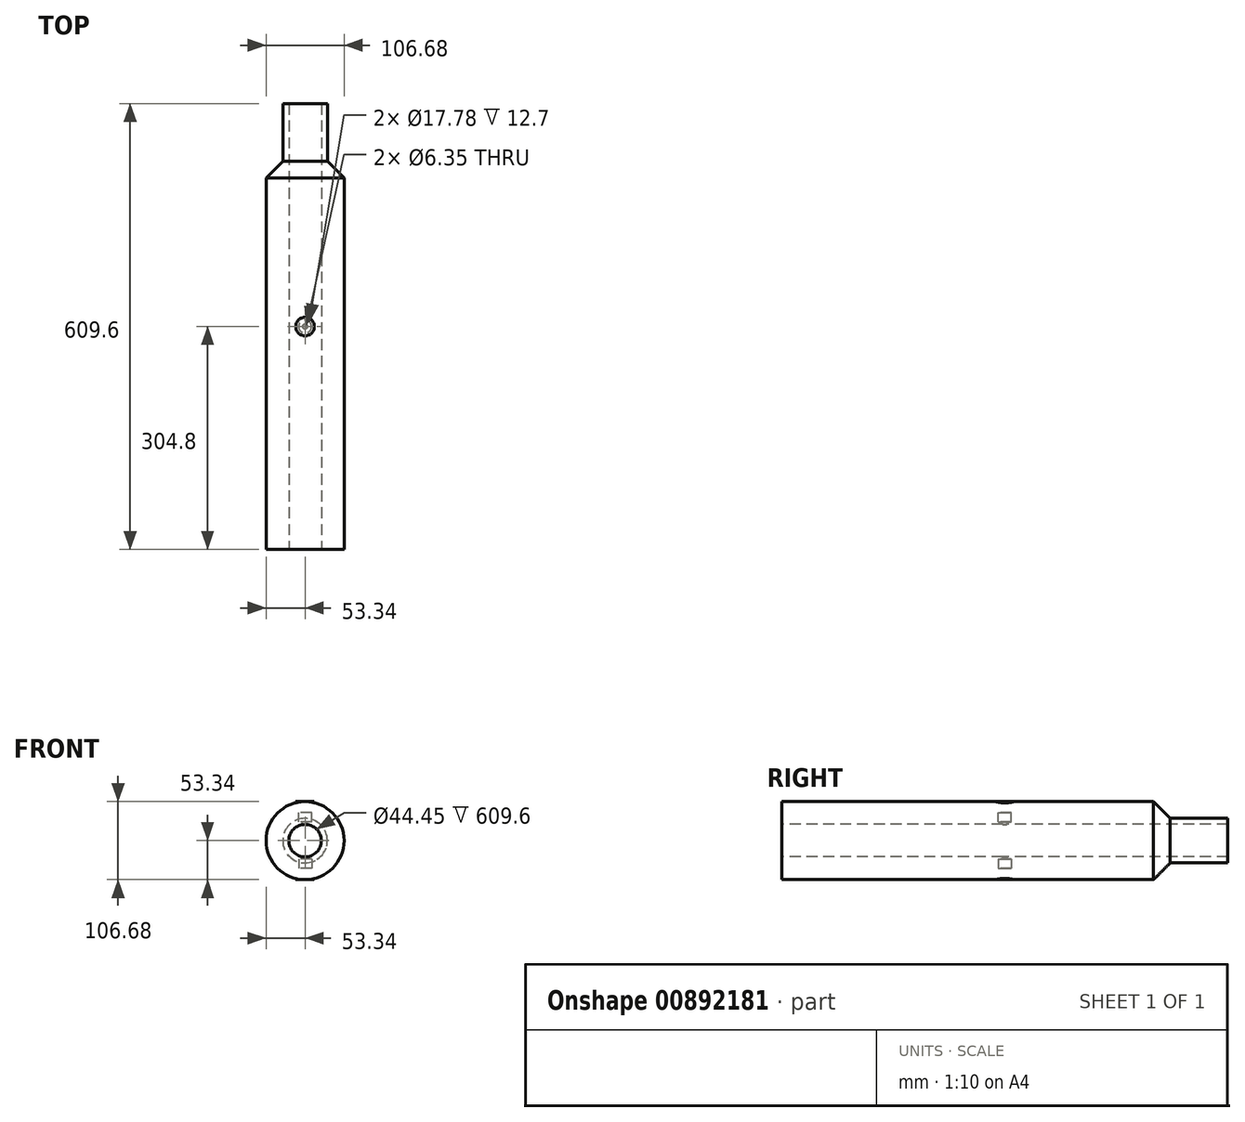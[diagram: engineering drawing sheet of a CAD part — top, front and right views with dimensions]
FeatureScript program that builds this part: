
annotation { "Feature Type Name" : "Feature", "Feature Type Description" : "" }
export const myFeature = defineFeature(function(context is Context, id is Id, definition is map)
    precondition{}
    {
        {
            var Q0;
            Q0=qCreatedBy(makeId("Front.planeOp"),FACE);
            var sketch = newSketch(context, id + "F0", { "sketchPlane" : qUnion([Q0])});
            skCircle(sketch, "E0", {"center": v(0, 0) * mm, "radius": 22.23 * mm});
            skCircle(sketch, "E1", {"center": v(0, 0) * mm, "radius": 53.34 * mm});
            skSolve(sketch);
        }
        {
            var Q0;
            Q0=makeQuery(id+"F0.imprint","IMPRINT",FACE,{"disambiguationData":[TD([[makeQuery(id+"F0.imprint","IMPRINT",EDGE,{"derivedFrom":sQuery(id+"F0.wireOp",EDGE,"E0")}),-1.0]])]});
            extrude(context, id + "F1", {"entities" : qUnion([Q0]), "endBound" : BoundingType.SYMMETRIC, "oppositeDirection" : true, "depth" : 609.6 * mm, "offsetDistance" : 25.4 * mm});
        }
        {
            var Q0;
            Q0=makeQuery(id+"F1.opExtrude","CAP_FACE",FACE,{"disambiguationData":[OSD([sQuery(id+"F0.wireOp",EDGE,"E0"),sQuery(id+"F0.wireOp",EDGE,"E1")])],"isStart":false});
            cPlane(context, id + "F2", {"entities" : qUnion([Q0]), "cplaneType" : CPlaneType.OFFSET, "offset" : 0 * mm, "oppositeDirection" : true, "width" : 152.4 * mm, "height" : 152.4 * mm});
        }
        {
            var Q0;
            Q0=qCreatedBy(makeId("Front.planeOp"),FACE);
            cPlane(context, id + "F3", {"entities" : qUnion([Q0]), "cplaneType" : CPlaneType.OFFSET, "offset" : 203.2 * mm, "oppositeDirection" : true, "width" : 152.4 * mm, "height" : 152.4 * mm});
        }
        {
            var Q0;
            Q0=qCreatedBy(id+"F2.planeOp",FACE);
            var sketch = newSketch(context, id + "F4", { "sketchPlane" : qUnion([Q0])});
            skCircle(sketch, "E2", {"center": v(0, 0) * mm, "radius": 22.23 * mm});
            skCircle(sketch, "E3", {"center": v(0, 0) * mm, "radius": 30.48 * mm});
            skCircle(sketch, "E4", {"center": v(0, 0) * mm, "radius": 53.34 * mm});
            skSolve(sketch);
        }
        {
            var Q0;
            Q0=makeQuery(id+"F4.imprint","IMPRINT",FACE,{"disambiguationData":[TD([[makeQuery(id+"F4.imprint","IMPRINT",EDGE,{"derivedFrom":sQuery(id+"F4.wireOp",EDGE,"E3")}),-1.0]])]});
            var Q1;
            Q1=qCreatedBy(id+"F3.planeOp",FACE);
            extrude(context, id + "F5", {"entities" : qUnion([Q0]), "operationType" : NewBodyOperationType.REMOVE, "oppositeDirection" : true, "depth" : 101.6 * mm, "endBoundEntityFace" : qUnion([Q1]), "offsetDistance" : 25.4 * mm});
        }
        {
            var Q0;
            Q0=qCreatedBy(makeId("Right.planeOp"),FACE);
            var sketch = newSketch(context, id + "F6", { "sketchPlane" : qUnion([Q0])});
            skLineSegment(sketch, "E5", {"start": v(0, 0) * mm, "end": v(203.2, 0) * mm, "construction": true});
            skLineSegment(sketch, "E6", {"start": v(203.2, 0) * mm, "end": v(203.2, 53.34) * mm});
            skLineSegment(sketch, "E7", {"start": v(203.2, 0) * mm, "end": v(203.2, 30.48) * mm});
            skLineSegment(sketch, "E8", {"start": v(203.2, 30.48) * mm, "end": v(226.06, 30.48) * mm});
            skLineSegment(sketch, "E9", {"start": v(226.06, 30.48) * mm, "end": v(203.2, 53.34) * mm});
            skSolve(sketch);
        }
        {
            var Q0;
            Q0=makeQuery(id+"F6.imprint","IMPRINT",FACE,{"disambiguationData":[TD([[makeQuery(id+"F6.imprint","IMPRINT",EDGE,{"derivedFrom":sQuery(id+"F6.wireOp",EDGE,"E6")}),-1.0]])]});
            var Q1;
            Q1=sQuery(id+"F6.wireOp",EDGE,"E5");
            revolve(context, id + "F7", {"operationType" : NewBodyOperationType.ADD, "surfaceOperationType" : NewSurfaceOperationType.NEW, "entities" : qUnion([Q0]), "axis" : qUnion([Q1]), "revolveType" : RevolveType.FULL});
        }
        {
            var Q0;
            Q0=qCreatedBy(makeId("Top.planeOp"),FACE);
            cPlane(context, id + "F8", {"entities" : qUnion([Q0]), "cplaneType" : CPlaneType.OFFSET, "offset" : 53.34 * mm, "width" : 152.4 * mm, "height" : 152.4 * mm});
        }
        {
            var Q0;
            Q0=qCreatedBy(makeId("Top.planeOp"),FACE);
            cPlane(context, id + "F9", {"entities" : qUnion([Q0]), "cplaneType" : CPlaneType.OFFSET, "offset" : 53.34 * mm, "oppositeDirection" : true, "width" : 152.4 * mm, "height" : 152.4 * mm});
        }
        {
            var Q0;
            Q0=qCreatedBy(id+"F8.planeOp",FACE);
            var sketch = newSketch(context, id + "F10", { "sketchPlane" : qUnion([Q0])});
            skCircle(sketch, "E10", {"center": v(0, 0) * mm, "radius": 12.7 * mm});
            skCircle(sketch, "E11", {"center": v(0, 0) * mm, "radius": 8.9 * mm});
            skCircle(sketch, "E12", {"center": v(0, 0) * mm, "radius": 3.18 * mm});
            skSolve(sketch);
        }
        {
            var Q0;
            Q0=makeQuery(id+"F10.imprint","IMPRINT",FACE,{"disambiguationData":[TD([[makeQuery(id+"F10.imprint","IMPRINT",EDGE,{"derivedFrom":sQuery(id+"F10.wireOp",EDGE,"E10")}),1.0]])]});
            var Q1;
            Q1=makeQuery(id+"F10.imprint","IMPRINT",FACE,{"disambiguationData":[TD([[makeQuery(id+"F10.imprint","IMPRINT",EDGE,{"derivedFrom":sQuery(id+"F10.wireOp",EDGE,"E12")}),1.0]])]});
            var Q2;
            Q2=makeQuery(id+"F10.imprint","IMPRINT",FACE,{"disambiguationData":[TD([[makeQuery(id+"F10.imprint","IMPRINT",EDGE,{"derivedFrom":sQuery(id+"F10.wireOp",EDGE,"E11")}),1.0]])]});
            extrude(context, id + "F11", {"entities" : qUnion([Q0, Q1, Q2]), "operationType" : NewBodyOperationType.REMOVE, "oppositeDirection" : true, "depth" : 15.24 * mm, "offsetDistance" : 25.4 * mm});
        }
        {
            var Q0;
            Q0=makeQuery(id+"F10.imprint","IMPRINT",FACE,{"disambiguationData":[TD([[makeQuery(id+"F10.imprint","IMPRINT",EDGE,{"derivedFrom":sQuery(id+"F10.wireOp",EDGE,"E11")}),1.0]])]});
            var Q1;
            Q1=makeQuery(id+"F10.imprint","IMPRINT",FACE,{"disambiguationData":[TD([[makeQuery(id+"F10.imprint","IMPRINT",EDGE,{"derivedFrom":sQuery(id+"F10.wireOp",EDGE,"E12")}),1.0]])]});
            extrude(context, id + "F12", {"entities" : qUnion([Q0, Q1]), "operationType" : NewBodyOperationType.REMOVE, "oppositeDirection" : true, "depth" : 27.94 * mm, "offsetDistance" : 25.4 * mm});
        }
        {
            var Q0;
            Q0=makeQuery(id+"F10.imprint","IMPRINT",FACE,{"disambiguationData":[TD([[makeQuery(id+"F10.imprint","IMPRINT",EDGE,{"derivedFrom":sQuery(id+"F10.wireOp",EDGE,"E12")}),1.0]])]});
            var Q1;
            Q1=makeQuery(id+"F1.opExtrude","SWEPT_FACE",FACE,{"disambiguationData":[OSD([sQuery(id+"F0.wireOp",EDGE,"E0")])]});
            extrude(context, id + "F13", {"entities" : qUnion([Q0]), "operationType" : NewBodyOperationType.REMOVE, "endBound" : BoundingType.UP_TO_SURFACE, "oppositeDirection" : true, "depth" : 53.34 * mm, "endBoundEntityFace" : qUnion([Q1]), "offsetDistance" : 25.4 * mm});
        }
        {
            var Q0;
            Q0=qCreatedBy(id+"F9.planeOp",FACE);
            var sketch = newSketch(context, id + "F14", { "sketchPlane" : qUnion([Q0])});
            skCircle(sketch, "E13", {"center": v(0, 0) * mm, "radius": 12.7 * mm});
            skCircle(sketch, "E14", {"center": v(0, 0) * mm, "radius": 8.9 * mm});
            skCircle(sketch, "E15", {"center": v(0, 0) * mm, "radius": 3.18 * mm});
            skSolve(sketch);
        }
        {
            var Q0;
            Q0=qSketchRegion(id+"F14",true);
            var Q1;
            Q1=makeQuery(id+"F14.imprint","IMPRINT",FACE,{"disambiguationData":[TD([[makeQuery(id+"F14.imprint","IMPRINT",EDGE,{"derivedFrom":sQuery(id+"F14.wireOp",EDGE,"E14")}),1.0]])]});
            var Q2;
            Q2=makeQuery(id+"F14.imprint","IMPRINT",FACE,{"disambiguationData":[TD([[makeQuery(id+"F14.imprint","IMPRINT",EDGE,{"derivedFrom":sQuery(id+"F14.wireOp",EDGE,"E15")}),1.0]])]});
            extrude(context, id + "F15", {"entities" : qUnion([Q0, Q1, Q2]), "operationType" : NewBodyOperationType.REMOVE, "depth" : 15.24 * mm, "offsetDistance" : 25.4 * mm});
        }
        {
            var Q0;
            Q0=makeQuery(id+"F14.imprint","IMPRINT",FACE,{"disambiguationData":[TD([[makeQuery(id+"F14.imprint","IMPRINT",EDGE,{"derivedFrom":sQuery(id+"F14.wireOp",EDGE,"E14")}),1.0]])]});
            var Q1;
            Q1=makeQuery(id+"F14.imprint","IMPRINT",FACE,{"disambiguationData":[TD([[makeQuery(id+"F14.imprint","IMPRINT",EDGE,{"derivedFrom":sQuery(id+"F14.wireOp",EDGE,"E15")}),1.0]])]});
            extrude(context, id + "F16", {"entities" : qUnion([Q0, Q1]), "operationType" : NewBodyOperationType.REMOVE, "depth" : 27.94 * mm, "offsetDistance" : 25.4 * mm});
        }
        {
            var Q0;
            Q0=makeQuery(id+"F14.imprint","IMPRINT",FACE,{"disambiguationData":[TD([[makeQuery(id+"F14.imprint","IMPRINT",EDGE,{"derivedFrom":sQuery(id+"F14.wireOp",EDGE,"E15")}),1.0]])]});
            var Q1;
            Q1=makeQuery(id+"F1.opExtrude","SWEPT_FACE",FACE,{"disambiguationData":[OSD([sQuery(id+"F0.wireOp",EDGE,"E0")])]});
            extrude(context, id + "F17", {"entities" : qUnion([Q0]), "operationType" : NewBodyOperationType.REMOVE, "endBound" : BoundingType.UP_TO_SURFACE, "depth" : 25.4 * mm, "endBoundEntityFace" : qUnion([Q1]), "offsetDistance" : 25.4 * mm});
        }
        {
            var Q0;
            Q0=qCreatedBy(id+"F8.planeOp",FACE);
            var sketch = newSketch(context, id + "F18", { "sketchPlane" : qUnion([Q0])});
            skCircle(sketch, "E16", {"center": v(0, 0) * mm, "radius": 12.7 * mm});
            skSolve(sketch);
        }
        {
            var Q0;
            Q0 = qSketchRegion(id + "F18", true);
            var Q1;
            Q1=makeQuery(id+"F11.boolean.opBoolean","COPY",FACE,{"derivedFrom":makeQuery(id+"F11.opExtrude","CAP_FACE",FACE,{"disambiguationData":[OSD([sQuery(id+"F10.wireOp",EDGE,"E10")])],"isStart":false})});
            extrude(context, id + "F19", {"entities" : qUnion([Q0]), "operationType" : NewBodyOperationType.ADD, "endBound" : BoundingType.UP_TO_SURFACE, "oppositeDirection" : true, "depth" : 15.24 * mm, "endBoundEntityFace" : qUnion([Q1]), "offsetDistance" : 25.4 * mm});
        }
        {
            var Q0;
            Q0=qCreatedBy(id+"F9.planeOp",FACE);
            var sketch = newSketch(context, id + "F20", { "sketchPlane" : qUnion([Q0])});
            skCircle(sketch, "E17", {"center": v(0, 0) * mm, "radius": 12.7 * mm});
            skSolve(sketch);
        }
        {
            var Q0;
            Q0 = qSketchRegion(id + "F20", true);
            var Q1;
            Q1=makeQuery(id+"F15.boolean.opBoolean","COPY",FACE,{"derivedFrom":makeQuery(id+"F15.opExtrude","CAP_FACE",FACE,{"disambiguationData":[OSD([sQuery(id+"F14.wireOp",EDGE,"E13")])],"isStart":false})});
            extrude(context, id + "F21", {"entities" : qUnion([Q0]), "operationType" : NewBodyOperationType.ADD, "endBound" : BoundingType.UP_TO_SURFACE, "depth" : 15.24 * mm, "endBoundEntityFace" : qUnion([Q1]), "offsetDistance" : 25.4 * mm});
        }
    });
